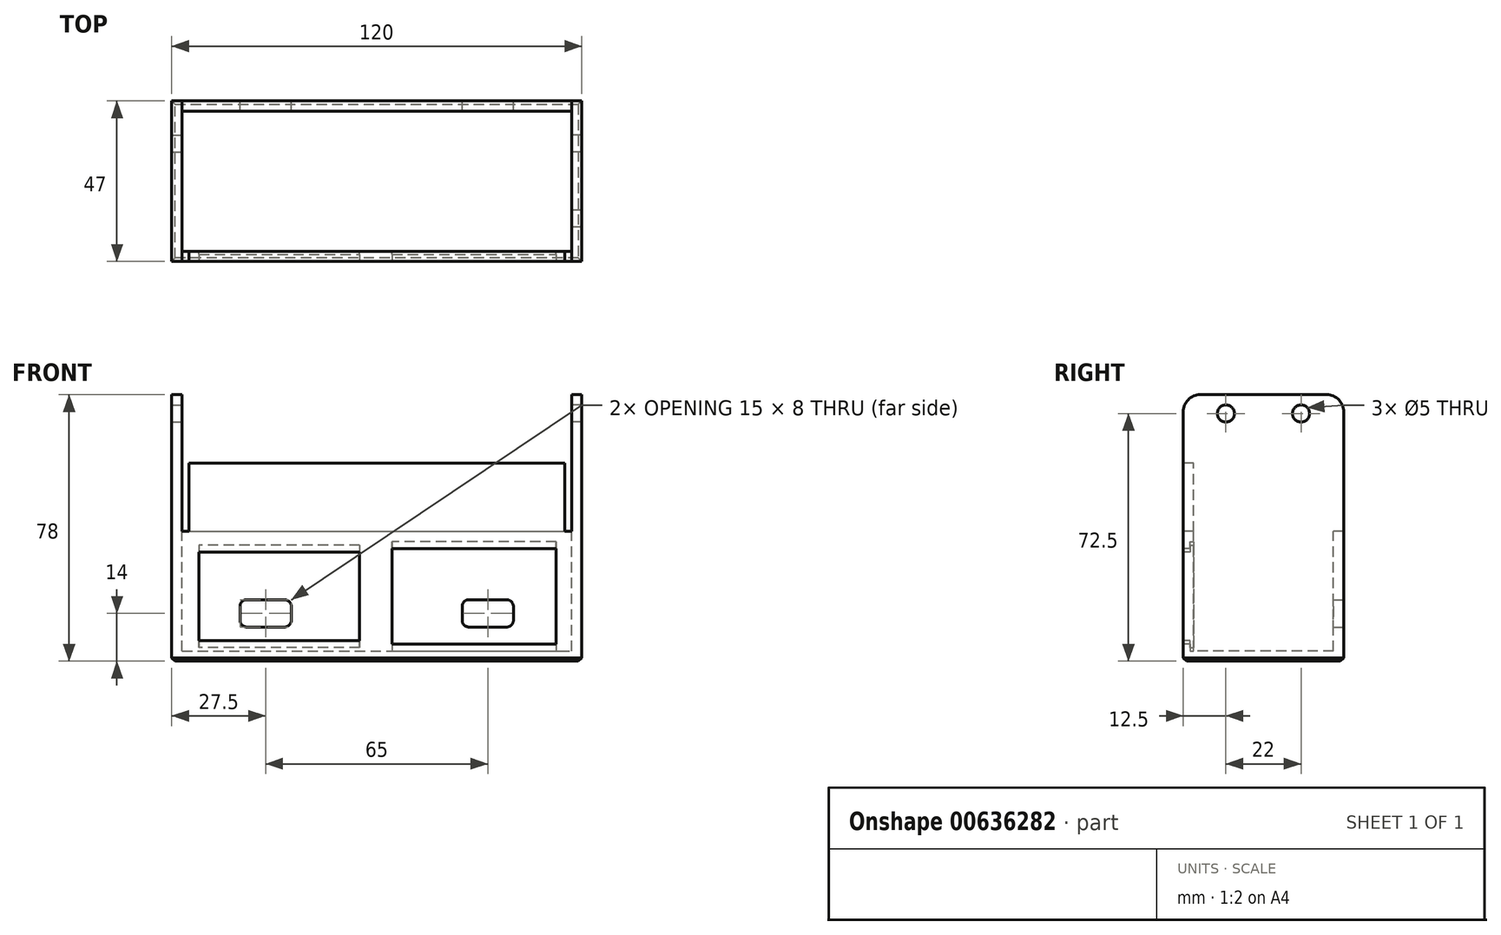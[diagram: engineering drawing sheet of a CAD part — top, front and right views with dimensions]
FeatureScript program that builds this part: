
annotation { "Feature Type Name" : "Feature", "Feature Type Description" : "" }
export const myFeature = defineFeature(function(context is Context, id is Id, definition is map)
    precondition{}
    {
        {
            assignVariable(context, id + "F0", {"name" : "wall", "anyValue" : 3});
        }
        {
            assignVariable(context, id + "F1", {"name" : "width", "anyValue" : 114});
        }
        {
            var Q0;
            Q0=qCreatedBy(makeId("Right.planeOp"),FACE);
            var sketch = newSketch(context, id + "F2", { "sketchPlane" : qUnion([Q0])});
            skLineSegment(sketch, "E0.bottom", {"start": v(17.5, 40) * mm, "end": v(-19.5, 40) * mm});
            skLineSegment(sketch, "E0.top", {"start": v(22.5, -38) * mm, "end": v(-24.5, -38) * mm});
            skLineSegment(sketch, "E0.left", {"start": v(22.5, 35) * mm, "end": v(22.5, -38) * mm});
            skLineSegment(sketch, "E0.right", {"start": v(-24.5, 35) * mm, "end": v(-24.5, -38) * mm});
            skCircle(sketch, "E1", {"center": v(10, 34.5) * mm, "radius": 2.5 * mm});
            skCircle(sketch, "E2", {"center": v(-12, 34.5) * mm, "radius": 2.5 * mm});
            skPoint(sketch, "E3.visualSharp", {"position": v(-24.5, 40) * mm});
            skArc(sketch, "E3.filletArc", {"start": v(-19.5, 40) * mm, "mid": v(-23.04, 38.54) * mm, "end": v(-24.5, 35) * mm});
            skPoint(sketch, "E4.visualSharp", {"position": v(22.5, 40) * mm});
            skArc(sketch, "E4.filletArc", {"start": v(22.5, 35) * mm, "mid": v(21.04, 38.54) * mm, "end": v(17.5, 40) * mm});
            skSolve(sketch);
        }
        {
            var Q0;
            Q0 = qSketchRegion(id + "F2", true);
            extrude(context, id + "F3", {"entities" : qUnion([Q0]), "depth" : (getVariable(context, 'wall')) * mm, "offsetDistance" : 25 * mm});
        }
        {
            var Q0;
            Q0=qCreatedBy(makeId("Right.planeOp"),FACE);
            var sketch = newSketch(context, id + "F4", { "sketchPlane" : qUnion([Q0])});
            skLineSegment(sketch, "E5.bottom", {"start": v(22.5, -38) * mm, "end": v(-24.5, -38) * mm});
            skLineSegment(sketch, "E5.top", {"start": v(22.5, -35) * mm, "end": v(-24.5, -35) * mm});
            skLineSegment(sketch, "E5.left", {"start": v(22.5, -38) * mm, "end": v(22.5, -35) * mm});
            skLineSegment(sketch, "E5.right", {"start": v(-24.5, -38) * mm, "end": v(-24.5, -35) * mm});
            skLineSegment(sketch, "E6.bottom", {"start": v(-24.5, -38) * mm, "end": v(-21.5, -38) * mm});
            skLineSegment(sketch, "E6.top", {"start": v(-24.5, 0) * mm, "end": v(-21.5, 0) * mm});
            skLineSegment(sketch, "E6.left", {"start": v(-24.5, -38) * mm, "end": v(-24.5, 0) * mm});
            skLineSegment(sketch, "E6.right", {"start": v(-21.5, -38) * mm, "end": v(-21.5, 0) * mm});
            skLineSegment(sketch, "E7.bottom", {"start": v(22.5, -38) * mm, "end": v(19.5, -38) * mm});
            skLineSegment(sketch, "E7.top", {"start": v(22.5, 0) * mm, "end": v(19.5, 0) * mm});
            skLineSegment(sketch, "E7.left", {"start": v(22.5, -38) * mm, "end": v(22.5, 0) * mm});
            skLineSegment(sketch, "E7.right", {"start": v(19.5, -38) * mm, "end": v(19.5, 0) * mm});
            skSolve(sketch);
        }
        {
            var Q0;
            Q0 = qSketchRegion(id + "F4", true);
            extrude(context, id + "F5", {"entities" : qUnion([Q0]), "operationType" : NewBodyOperationType.ADD, "oppositeDirection" : true, "depth" : (getVariable(context, 'width')) * mm, "offsetDistance" : 25 * mm});
        }
        {
            var Q0;
            Q0=makeQuery(id+"F5.opExtrude","CAP_FACE",FACE,{"disambiguationData":[OSD([sQuery(id+"F4.wireOp",EDGE,"E5.bottom"),sQuery(id+"F4.wireOp",EDGE,"E5.top"),sQuery(id+"F4.wireOp",EDGE,"E6.bottom"),sQuery(id+"F4.wireOp",EDGE,"E6.top"),sQuery(id+"F4.wireOp",EDGE,"E6.left"),sQuery(id+"F4.wireOp",EDGE,"E6.right"),sQuery(id+"F4.wireOp",EDGE,"E7.bottom"),sQuery(id+"F4.wireOp",EDGE,"E7.top"),sQuery(id+"F4.wireOp",EDGE,"E7.left"),sQuery(id+"F4.wireOp",EDGE,"E7.right")])],"isStart":false});
            var sketch = newSketch(context, id + "F6", { "sketchPlane" : qUnion([Q0])});
            skLineSegment(sketch, "E8.bottom", {"start": v(19.5, 40) * mm, "end": v(-17.5, 40) * mm});
            skLineSegment(sketch, "E8.top", {"start": v(24.5, -38) * mm, "end": v(-22.5, -38) * mm});
            skLineSegment(sketch, "E8.left", {"start": v(24.5, 35) * mm, "end": v(24.5, -38) * mm});
            skLineSegment(sketch, "E8.right", {"start": v(-22.5, 35) * mm, "end": v(-22.5, -38) * mm});
            skCircle(sketch, "E9", {"center": v(-10, 34.5) * mm, "radius": 2.5 * mm});
            skPoint(sketch, "E10.visualSharp", {"position": v(-22.5, 40) * mm});
            skArc(sketch, "E10.filletArc", {"start": v(-17.5, 40) * mm, "mid": v(-21.04, 38.54) * mm, "end": v(-22.5, 35) * mm});
            skPoint(sketch, "E11.visualSharp", {"position": v(24.5, 40) * mm});
            skArc(sketch, "E11.filletArc", {"start": v(24.5, 35) * mm, "mid": v(23.04, 38.54) * mm, "end": v(19.5, 40) * mm});
            skSolve(sketch);
        }
        {
            var Q0;
            Q0 = qSketchRegion(id + "F6", true);
            extrude(context, id + "F7", {"entities" : qUnion([Q0]), "operationType" : NewBodyOperationType.ADD, "depth" : (getVariable(context, 'wall')) * mm, "offsetDistance" : 25 * mm});
        }
        {
            var Q0;
            Q0=makeQuery(id+"F7.boolean.opBoolean","MERGE",FACE,{"derivedFrom":[makeQuery(id+"F5.boolean.opBoolean","MERGE",FACE,{"derivedFrom":[makeQuery(id+"F3.opExtrude","SWEPT_FACE",FACE,{"disambiguationData":[OSD([sQuery(id+"F2.wireOp",EDGE,"E0.right")])]}),makeQuery(id+"F5.opExtrude","SWEPT_FACE",FACE,{"disambiguationData":[OSD([sQuery(id+"F4.wireOp",EDGE,"E6.left")])]})]}),makeQuery(id+"F7.opExtrude","SWEPT_FACE",FACE,{"disambiguationData":[OSD([sQuery(id+"F6.wireOp",EDGE,"E8.left")])]})]});
            var sketch = newSketch(context, id + "F8", { "sketchPlane" : qUnion([Q0])});
            skLineSegment(sketch, "E12.bottom", {"start": v(-112, 0) * mm, "end": v(-2, 0) * mm});
            skLineSegment(sketch, "E12.top", {"start": v(-112, 20) * mm, "end": v(-2, 20) * mm});
            skLineSegment(sketch, "E12.left", {"start": v(-112, 0) * mm, "end": v(-112, 20) * mm});
            skLineSegment(sketch, "E12.right", {"start": v(-2, 0) * mm, "end": v(-2, 20) * mm});
            skSolve(sketch);
        }
        {
            var Q0;
            Q0 = qSketchRegion(id + "F8", true);
            extrude(context, id + "F9", {"entities" : qUnion([Q0]), "operationType" : NewBodyOperationType.ADD, "oppositeDirection" : true, "depth" : (getVariable(context, 'wall')) * mm, "offsetDistance" : 25 * mm});
        }
        {
            var Q0;
            {var subQ2=sQuery(id+"F8.wireOp",EDGE,"E12.bottom");Q0=makeQuery(id+"F8.imprint","IMPRINT",FACE,{"disambiguationData":[TD([[makeQuery(id+"F8.imprint","IMPRINT",EDGE,{"derivedFrom":subQ2}),-1.0]])]});}
            var sketch = newSketch(context, id + "F10", { "sketchPlane" : qUnion([Q0])});
            skLineSegment(sketch, "E13.bottom", {"start": v(-109, -6) * mm, "end": v(-62, -6) * mm});
            skLineSegment(sketch, "E13.top", {"start": v(-109, -32) * mm, "end": v(-62, -32) * mm});
            skLineSegment(sketch, "E13.left", {"start": v(-109, -6) * mm, "end": v(-109, -32) * mm});
            skLineSegment(sketch, "E13.right", {"start": v(-62, -6) * mm, "end": v(-62, -32) * mm});
            skLineSegment(sketch, "E14.bottom", {"start": v(-52.5, -5) * mm, "end": v(-4.5, -5) * mm});
            skLineSegment(sketch, "E14.top", {"start": v(-52.5, -33) * mm, "end": v(-4.5, -33) * mm});
            skLineSegment(sketch, "E14.left", {"start": v(-52.5, -5) * mm, "end": v(-52.5, -33) * mm});
            skLineSegment(sketch, "E14.right", {"start": v(-4.5, -5) * mm, "end": v(-4.5, -33) * mm});
            skLineSegment(sketch, "E15", {"start": v(-57, 0) * mm, "end": v(-57, -48.8) * mm, "construction": true});
            skLineSegment(sketch, "E16", {"start": v(-121.46, -19) * mm, "end": v(11.47, -19) * mm, "construction": true});
            skSolve(sketch);
        }
        {
            var Q0;
            Q0 = qSketchRegion(id + "F10", true);
            extrude(context, id + "F11", {"entities" : qUnion([Q0]), "operationType" : NewBodyOperationType.REMOVE, "endBound" : BoundingType.UP_TO_NEXT, "oppositeDirection" : true, "depth" : 25 * mm, "offsetDistance" : 25 * mm});
        }
        {
            var Q0;
            Q0=makeQuery(id+"F7.boolean.opBoolean","MERGE",FACE,{"derivedFrom":[makeQuery(id+"F5.boolean.opBoolean","MERGE",FACE,{"derivedFrom":[makeQuery(id+"F3.opExtrude","SWEPT_FACE",FACE,{"disambiguationData":[OSD([sQuery(id+"F2.wireOp",EDGE,"E0.left")])]}),makeQuery(id+"F5.opExtrude","SWEPT_FACE",FACE,{"disambiguationData":[OSD([sQuery(id+"F4.wireOp",EDGE,"E7.left")])]})]}),makeQuery(id+"F7.opExtrude","SWEPT_FACE",FACE,{"disambiguationData":[OSD([sQuery(id+"F6.wireOp",EDGE,"E8.right")])]})]});
            var sketch = newSketch(context, id + "F12", { "sketchPlane" : qUnion([Q0])});
            skLineSegment(sketch, "E17.bottom", {"start": v(84, -28) * mm, "end": v(95, -28) * mm});
            skLineSegment(sketch, "E17.top", {"start": v(84, -20) * mm, "end": v(95, -20) * mm});
            skLineSegment(sketch, "E17.left", {"start": v(82, -26) * mm, "end": v(82, -22) * mm});
            skLineSegment(sketch, "E17.right", {"start": v(97, -26) * mm, "end": v(97, -22) * mm});
            skPoint(sketch, "E18.visualSharp", {"position": v(82, -28) * mm});
            skArc(sketch, "E18.filletArc", {"start": v(82, -26) * mm, "mid": v(82.59, -27.41) * mm, "end": v(84, -28) * mm});
            skPoint(sketch, "E19.visualSharp", {"position": v(82, -20) * mm});
            skArc(sketch, "E19.filletArc", {"start": v(84, -20) * mm, "mid": v(82.59, -20.59) * mm, "end": v(82, -22) * mm});
            skPoint(sketch, "E20.visualSharp", {"position": v(97, -20) * mm});
            skArc(sketch, "E20.filletArc", {"start": v(97, -22) * mm, "mid": v(96.41, -20.59) * mm, "end": v(95, -20) * mm});
            skPoint(sketch, "E21.visualSharp", {"position": v(97, -28) * mm});
            skArc(sketch, "E21.filletArc", {"start": v(95, -28) * mm, "mid": v(96.41, -27.41) * mm, "end": v(97, -26) * mm});
            skArc(sketch, "E22.MirrorCS", {"start": v(19, -28) * mm, "mid": v(17.59, -27.41) * mm, "end": v(17, -26) * mm});
            skArc(sketch, "E23.MirrorCS", {"start": v(17, -22) * mm, "mid": v(17.59, -20.59) * mm, "end": v(19, -20) * mm});
            skArc(sketch, "E24.MirrorCS", {"start": v(30, -20) * mm, "mid": v(31.41, -20.59) * mm, "end": v(32, -22) * mm});
            skArc(sketch, "E25.MirrorCS", {"start": v(32, -26) * mm, "mid": v(31.41, -27.41) * mm, "end": v(30, -28) * mm});
            skLineSegment(sketch, "E26.MirrorCS", {"start": v(17, -26) * mm, "end": v(17, -22) * mm});
            skLineSegment(sketch, "E27.MirrorCS", {"start": v(32, -26) * mm, "end": v(32, -22) * mm});
            skPoint(sketch, "E28.MirrorP", {"position": v(17, -20) * mm});
            skPoint(sketch, "E29.MirrorP", {"position": v(32, -20) * mm});
            skPoint(sketch, "E30.MirrorP", {"position": v(32, -28) * mm});
            skLineSegment(sketch, "E31.MirrorCS", {"start": v(30, -28) * mm, "end": v(19, -28) * mm});
            skLineSegment(sketch, "E32.MirrorCS", {"start": v(30, -20) * mm, "end": v(19, -20) * mm});
            skPoint(sketch, "E33.MirrorP", {"position": v(17, -28) * mm});
            skSolve(sketch);
        }
        {
            var Q0;
            Q0 = qSketchRegion(id + "F12", true);
            extrude(context, id + "F13", {"entities" : qUnion([Q0]), "operationType" : NewBodyOperationType.REMOVE, "endBound" : BoundingType.UP_TO_NEXT, "oppositeDirection" : true, "depth" : 25 * mm, "offsetDistance" : 25 * mm});
        }
        {
            var Q0;
            Q0=makeQuery(id+"F7.boolean.opBoolean","MERGE",FACE,{"derivedFrom":[makeQuery(id+"F5.boolean.opBoolean","MERGE",FACE,{"derivedFrom":[makeQuery(id+"F3.opExtrude","SWEPT_FACE",FACE,{"disambiguationData":[OSD([sQuery(id+"F2.wireOp",EDGE,"E0.top")])]}),makeQuery(id+"F5.opExtrude","SWEPT_FACE",FACE,{"disambiguationData":[OSD([sQuery(id+"F4.wireOp",EDGE,"E5.bottom"),sQuery(id+"F4.wireOp",EDGE,"E6.bottom"),sQuery(id+"F4.wireOp",EDGE,"E7.bottom")])]})]}),makeQuery(id+"F7.opExtrude","SWEPT_FACE",FACE,{"disambiguationData":[OSD([sQuery(id+"F6.wireOp",EDGE,"E8.top")])]})]});
            chamfer(context, id + "F14", {"entities" : qUnion([Q0]), "width" : 1 * mm, "tangentPropagation" : true});
        }
        {
            assignVariable(context, id + "F15", {"name" : "InsertClipD", "anyValue" : 1});
        }
        {
            var Q0;
            Q0=makeQuery(id+"F9.boolean.opBoolean","MERGE",FACE,{"derivedFrom":[makeQuery(id+"F5.opExtrude","SWEPT_FACE",FACE,{"disambiguationData":[OSD([sQuery(id+"F4.wireOp",EDGE,"E6.right")])]}),makeQuery(id+"F9.opExtrude","CAP_FACE",FACE,{"disambiguationData":[OSD([sQuery(id+"F8.wireOp",EDGE,"E12.bottom"),sQuery(id+"F8.wireOp",EDGE,"E12.top"),sQuery(id+"F8.wireOp",EDGE,"E12.left"),sQuery(id+"F8.wireOp",EDGE,"E12.right")])],"isStart":false})]});
            var sketch = newSketch(context, id + "F16", { "sketchPlane" : qUnion([Q0])});
            skLineSegment(sketch, "E34.bottom", {"start": v(4.5, -5) * mm, "end": v(52.5, -5) * mm});
            skLineSegment(sketch, "E34.top", {"start": v(4.5, -3) * mm, "end": v(52.5, -3) * mm});
            skLineSegment(sketch, "E34.left", {"start": v(4.5, -5) * mm, "end": v(4.5, -3) * mm});
            skLineSegment(sketch, "E34.right", {"start": v(52.5, -5) * mm, "end": v(52.5, -3) * mm});
            skLineSegment(sketch, "E35.bottom", {"start": v(4.5, -33) * mm, "end": v(52.5, -33) * mm});
            skLineSegment(sketch, "E35.top", {"start": v(4.5, -35) * mm, "end": v(52.5, -35) * mm});
            skLineSegment(sketch, "E35.left", {"start": v(4.5, -33) * mm, "end": v(4.5, -35) * mm});
            skLineSegment(sketch, "E35.right", {"start": v(52.5, -33) * mm, "end": v(52.5, -35) * mm});
            skLineSegment(sketch, "E36.bottom", {"start": v(62, -4) * mm, "end": v(109, -4) * mm});
            skLineSegment(sketch, "E36.top", {"start": v(62, -6) * mm, "end": v(109, -6) * mm});
            skLineSegment(sketch, "E36.left", {"start": v(62, -4) * mm, "end": v(62, -6) * mm});
            skLineSegment(sketch, "E36.right", {"start": v(109, -4) * mm, "end": v(109, -6) * mm});
            skLineSegment(sketch, "E37.bottom", {"start": v(62, -34) * mm, "end": v(109, -34) * mm});
            skLineSegment(sketch, "E37.top", {"start": v(62, -32) * mm, "end": v(109, -32) * mm});
            skLineSegment(sketch, "E37.left", {"start": v(62, -34) * mm, "end": v(62, -32) * mm});
            skLineSegment(sketch, "E37.right", {"start": v(109, -34) * mm, "end": v(109, -32) * mm});
            skSolve(sketch);
        }
        {
            var Q0;
            Q0=makeQuery(id+"F16.imprint","IMPRINT",FACE,{"disambiguationData":[TD([[makeQuery(id+"F16.imprint","IMPRINT",EDGE,{"derivedFrom":sQuery(id+"F16.wireOp",EDGE,"E35.bottom")}),1.0]])]});
            var Q1;
            Q1=makeQuery(id+"F16.imprint","IMPRINT",FACE,{"disambiguationData":[TD([[makeQuery(id+"F16.imprint","IMPRINT",EDGE,{"derivedFrom":sQuery(id+"F16.wireOp",EDGE,"E37.bottom")}),1.0]])]});
            var Q2;
            Q2=makeQuery(id+"F16.imprint","IMPRINT",FACE,{"disambiguationData":[TD([[makeQuery(id+"F16.imprint","IMPRINT",EDGE,{"derivedFrom":sQuery(id+"F16.wireOp",EDGE,"E36.bottom")}),-1.0]])]});
            var Q3;
            Q3=makeQuery(id+"F16.imprint","IMPRINT",FACE,{"disambiguationData":[TD([[makeQuery(id+"F16.imprint","IMPRINT",EDGE,{"derivedFrom":sQuery(id+"F16.wireOp",EDGE,"E34.bottom")}),-1.0]])]});
            extrude(context, id + "F17", {"entities" : qUnion([Q0, Q1, Q2, Q3]), "operationType" : NewBodyOperationType.REMOVE, "oppositeDirection" : true, "depth" : (getVariable(context, 'InsertClipD')) * mm, "offsetDistance" : 25 * mm});
        }
    });
